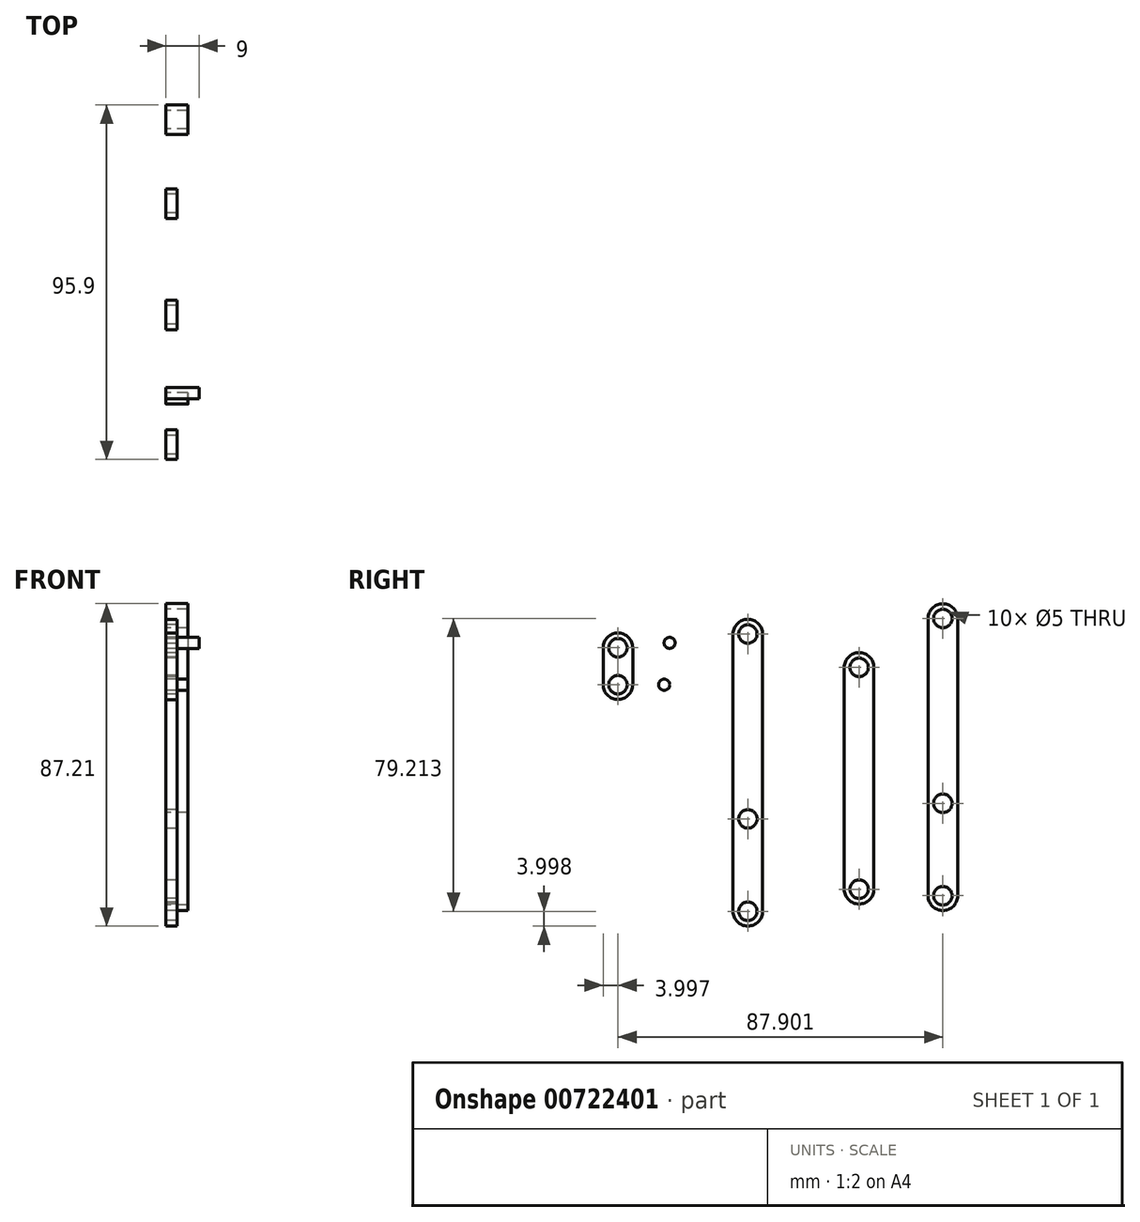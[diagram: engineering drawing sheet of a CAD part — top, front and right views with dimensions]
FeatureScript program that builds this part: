
annotation { "Feature Type Name" : "Feature", "Feature Type Description" : "" }
export const myFeature = defineFeature(function(context is Context, id is Id, definition is map)
    precondition{}
    {
        {
            var Q0;
            Q0=qCreatedBy(makeId("Right.planeOp"),FACE);
            var sketch = newSketch(context, id + "F0", { "sketchPlane" : qUnion([Q0])});
            skArc(sketch, "E0", {"start": v(-49.34, 38.54) * mm, "mid": v(-53.34, 42.54) * mm, "end": v(-57.34, 38.54) * mm});
            skArc(sketch, "E1", {"start": v(-57.34, 28.54) * mm, "mid": v(-53.34, 24.54) * mm, "end": v(-49.34, 28.54) * mm});
            skLineSegment(sketch, "E2", {"start": v(-57.34, 38.54) * mm, "end": v(-57.34, 28.54) * mm});
            skLineSegment(sketch, "E3", {"start": v(-49.34, 39.3) * mm, "end": v(-49.34, 28.54) * mm});
            skCircle(sketch, "E4", {"center": v(-53.34, 38.54) * mm, "radius": 2.5 * mm});
            skCircle(sketch, "E5", {"center": v(-53.34, 28.54) * mm, "radius": 2.5 * mm});
            skSolve(sketch);
        }
        {
            var Q0;
            {var subQ1=sQuery(id+"F0.wireOp",EDGE,"E0");Q0=makeQuery(id+"F0.imprint","IMPRINT",FACE,{"disambiguationData":[TD([[makeQuery(id+"F0.imprint","IMPRINT",EDGE,{"derivedFrom":subQ1}),1.0]])]});}
            extrude(context, id + "F1", {"entities" : qUnion([Q0]), "depth" : 3 * mm, "offsetDistance" : 25 * mm});
        }
        {
            var Q0;
            Q0=qCreatedBy(makeId("Right.planeOp"),FACE);
            var sketch = newSketch(context, id + "F2", { "sketchPlane" : qUnion([Q0])});
            skCircle(sketch, "E6", {"center": v(-39.38, 39.86) * mm, "radius": 1.5 * mm});
            skSolve(sketch);
        }
        {
            var Q0;
            Q0=makeQuery(id+"F2.imprint","IMPRINT",FACE,{"disambiguationData":[TD([[makeQuery(id+"F2.imprint","IMPRINT",EDGE,{"derivedFrom":sQuery(id+"F2.wireOp",EDGE,"E6")}),1.0]])]});
            extrude(context, id + "F3", {"entities" : qUnion([Q0]), "depth" : 9 * mm, "offsetDistance" : 25 * mm});
        }
        {
            var Q0;
            Q0=qCreatedBy(makeId("Right.planeOp"),FACE);
            var sketch = newSketch(context, id + "F4", { "sketchPlane" : qUnion([Q0])});
            skArc(sketch, "E7", {"start": v(-14.2, 42.25) * mm, "mid": v(-18.2, 46.25) * mm, "end": v(-22.2, 42.25) * mm});
            skArc(sketch, "E8", {"start": v(-22.2, -32.75) * mm, "mid": v(-18.2, -36.75) * mm, "end": v(-14.2, -32.75) * mm});
            skLineSegment(sketch, "E9", {"start": v(-22.2, -32.75) * mm, "end": v(-22.2, 42.25) * mm});
            skLineSegment(sketch, "E10", {"start": v(-14.2, -32.75) * mm, "end": v(-14.2, 42.25) * mm});
            skCircle(sketch, "E11", {"center": v(-18.2, 42.25) * mm, "radius": 2.5 * mm});
            skCircle(sketch, "E12", {"center": v(-18.2, -32.75) * mm, "radius": 2.5 * mm});
            skCircle(sketch, "E13", {"center": v(-18.18, -7.75) * mm, "radius": 2.5 * mm});
            skSolve(sketch);
        }
        {
            var Q0;
            Q0=makeQuery(id+"F4.imprint","IMPRINT",FACE,{"disambiguationData":[TD([[makeQuery(id+"F4.imprint","IMPRINT",EDGE,{"derivedFrom":sQuery(id+"F4.wireOp",EDGE,"E7")}),1.0]])]});
            extrude(context, id + "F5", {"entities" : qUnion([Q0]), "depth" : 3 * mm, "offsetDistance" : 25 * mm});
        }
        {
            var Q0;
            Q0=qCreatedBy(makeId("Right.planeOp"),FACE);
            var sketch = newSketch(context, id + "F6", { "sketchPlane" : qUnion([Q0])});
            skArc(sketch, "E14", {"start": v(15.9, 33.24) * mm, "mid": v(11.9, 37.24) * mm, "end": v(7.9, 33.24) * mm});
            skArc(sketch, "E15", {"start": v(7.9, -26.76) * mm, "mid": v(11.9, -30.76) * mm, "end": v(15.9, -26.76) * mm});
            skLineSegment(sketch, "E16", {"start": v(7.9, 33.24) * mm, "end": v(7.9, -26.76) * mm});
            skLineSegment(sketch, "E17", {"start": v(15.9, 33.24) * mm, "end": v(15.9, -26.76) * mm});
            skCircle(sketch, "E18", {"center": v(11.9, 33.24) * mm, "radius": 2.5 * mm});
            skCircle(sketch, "E19", {"center": v(11.9, -26.76) * mm, "radius": 2.5 * mm});
            skSolve(sketch);
        }
        {
            var Q0;
            Q0=makeQuery(id+"F6.imprint","IMPRINT",FACE,{"disambiguationData":[TD([[makeQuery(id+"F6.imprint","IMPRINT",EDGE,{"derivedFrom":sQuery(id+"F6.wireOp",EDGE,"E14")}),1.0]])]});
            extrude(context, id + "F7", {"entities" : qUnion([Q0]), "depth" : 3 * mm, "offsetDistance" : 25 * mm});
        }
        {
            var Q0;
            Q0=qCreatedBy(makeId("Right.planeOp"),FACE);
            var sketch = newSketch(context, id + "F8", { "sketchPlane" : qUnion([Q0])});
            skArc(sketch, "E20", {"start": v(38.56, 46.46) * mm, "mid": v(34.56, 50.46) * mm, "end": v(30.56, 46.46) * mm});
            skArc(sketch, "E21", {"start": v(30.56, -28.54) * mm, "mid": v(34.56, -32.54) * mm, "end": v(38.56, -28.54) * mm});
            skCircle(sketch, "E22", {"center": v(34.56, -3.54) * mm, "radius": 2.5 * mm});
            skLineSegment(sketch, "E23", {"start": v(30.56, 46.46) * mm, "end": v(30.56, -28.54) * mm});
            skLineSegment(sketch, "E24", {"start": v(38.56, 46.46) * mm, "end": v(38.56, -28.54) * mm});
            skCircle(sketch, "E25", {"center": v(34.56, 46.46) * mm, "radius": 2.5 * mm});
            skCircle(sketch, "E26", {"center": v(34.56, -28.54) * mm, "radius": 2.5 * mm});
            skSolve(sketch);
        }
        {
            var Q0;
            Q0=makeQuery(id+"F8.imprint","IMPRINT",FACE,{"disambiguationData":[TD([[makeQuery(id+"F8.imprint","IMPRINT",EDGE,{"derivedFrom":sQuery(id+"F8.wireOp",EDGE,"E20")}),1.0]])]});
            extrude(context, id + "F9", {"entities" : qUnion([Q0]), "depth" : 6 * mm, "offsetDistance" : 25 * mm});
        }
        {
            var Q0;
            Q0=qCreatedBy(makeId("Right.planeOp"),FACE);
            var sketch = newSketch(context, id + "F10", { "sketchPlane" : qUnion([Q0])});
            skCircle(sketch, "E27", {"center": v(-40.82, 28.54) * mm, "radius": 1.5 * mm});
            skSolve(sketch);
        }
        {
            var Q0;
            Q0=makeQuery(id+"F10.imprint","IMPRINT",FACE,{"disambiguationData":[TD([[makeQuery(id+"F10.imprint","IMPRINT",EDGE,{"derivedFrom":sQuery(id+"F10.wireOp",EDGE,"E27")}),1.0]])]});
            extrude(context, id + "F11", {"entities" : qUnion([Q0]), "depth" : 6 * mm, "offsetDistance" : 25 * mm});
        }
    });
